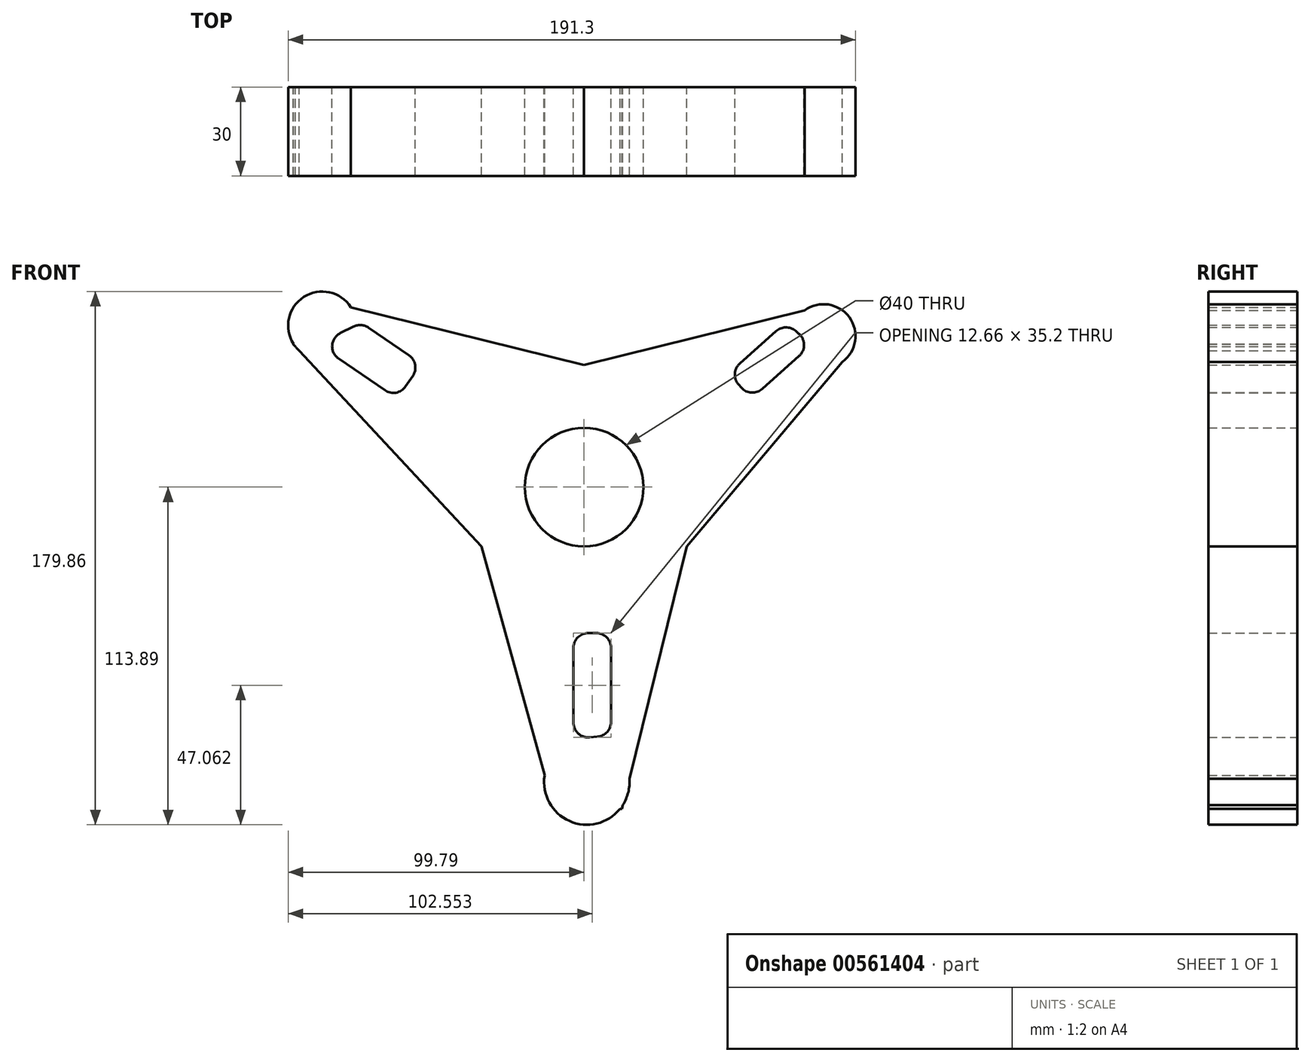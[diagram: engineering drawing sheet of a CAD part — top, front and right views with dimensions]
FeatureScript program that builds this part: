
annotation { "Feature Type Name" : "Feature", "Feature Type Description" : "" }
export const myFeature = defineFeature(function(context is Context, id is Id, definition is map)
    precondition{}
    {
        {
            var Q0;
            Q0=qCreatedBy(makeId("Front.planeOp"),FACE);
            var sketch = newSketch(context, id + "F0", { "sketchPlane" : qUnion([Q0])});
            skCircle(sketch, "E0", {"center": v(0, 0) * mm, "radius": 20 * mm});
            skCircle(sketch, "E1", {"center": v(0, 0) * mm, "radius": 40 * mm});
            skLineSegment(sketch, "E2", {"start": v(-3.57, -54.23) * mm, "end": v(-3.57, -79.44) * mm});
            skLineSegment(sketch, "E3", {"start": v(1.43, -49.23) * mm, "end": v(4.1, -49.23) * mm});
            skLineSegment(sketch, "E4", {"start": v(9.1, -54.23) * mm, "end": v(9.1, -79.23) * mm});
            skLineSegment(sketch, "E5", {"start": v(4.5, -84.21) * mm, "end": v(1.84, -84.43) * mm});
            skPoint(sketch, "E6.visualSharp", {"position": v(-3.57, -49.23) * mm});
            skArc(sketch, "E6.filletArc", {"start": v(1.43, -49.23) * mm, "mid": v(-2.1, -50.7) * mm, "end": v(-3.57, -54.23) * mm});
            skPoint(sketch, "E7.visualSharp", {"position": v(9.1, -49.23) * mm});
            skArc(sketch, "E7.filletArc", {"start": v(9.1, -54.23) * mm, "mid": v(7.63, -50.7) * mm, "end": v(4.1, -49.23) * mm});
            skPoint(sketch, "E8.visualSharp", {"position": v(9.1, -83.84) * mm});
            skArc(sketch, "E8.filletArc", {"start": v(4.5, -84.21) * mm, "mid": v(7.77, -82.62) * mm, "end": v(9.1, -79.23) * mm});
            skPoint(sketch, "E9.visualSharp", {"position": v(-3.57, -84.87) * mm});
            skArc(sketch, "E9.filletArc", {"start": v(-3.57, -79.44) * mm, "mid": v(-1.96, -83.12) * mm, "end": v(1.84, -84.43) * mm});
            skLineSegment(sketch, "E10", {"start": v(-72.68, 53.8) * mm, "end": v(-59.06, 44.46) * mm});
            skLineSegment(sketch, "E11", {"start": v(-57.76, 37.5) * mm, "end": v(-60.21, 33.94) * mm});
            skLineSegment(sketch, "E12", {"start": v(-67.17, 32.64) * mm, "end": v(-82.78, 43.35) * mm});
            skLineSegment(sketch, "E13", {"start": v(-82.17, 51.95) * mm, "end": v(-77.73, 54.16) * mm});
            skLineSegment(sketch, "E14", {"start": v(64.75, 52.59) * mm, "end": v(52.5, 41.65) * mm});
            skLineSegment(sketch, "E15", {"start": v(52.1, 34.6) * mm, "end": v(53.04, 33.54) * mm});
            skLineSegment(sketch, "E16", {"start": v(60.1, 33.14) * mm, "end": v(72.5, 44.22) * mm});
            skLineSegment(sketch, "E17", {"start": v(72.37, 51.8) * mm, "end": v(71.28, 52.7) * mm});
            skPoint(sketch, "E18.visualSharp", {"position": v(-75.1, 55.46) * mm});
            skArc(sketch, "E18.filletArc", {"start": v(-72.68, 53.8) * mm, "mid": v(-75.16, 54.67) * mm, "end": v(-77.73, 54.16) * mm});
            skPoint(sketch, "E19.visualSharp", {"position": v(-89.8, 48.17) * mm});
            skArc(sketch, "E19.filletArc", {"start": v(-82.17, 51.95) * mm, "mid": v(-84.94, 47.82) * mm, "end": v(-82.78, 43.35) * mm});
            skPoint(sketch, "E20.visualSharp", {"position": v(-63.04, 29.81) * mm});
            skArc(sketch, "E20.filletArc", {"start": v(-67.17, 32.64) * mm, "mid": v(-63.42, 31.85) * mm, "end": v(-60.21, 33.94) * mm});
            skPoint(sketch, "E21.visualSharp", {"position": v(-54.94, 41.63) * mm});
            skArc(sketch, "E21.filletArc", {"start": v(-57.76, 37.5) * mm, "mid": v(-56.97, 41.25) * mm, "end": v(-59.06, 44.46) * mm});
            skPoint(sketch, "E22.visualSharp", {"position": v(48.77, 38.32) * mm});
            skArc(sketch, "E22.filletArc", {"start": v(52.5, 41.65) * mm, "mid": v(50.84, 38.2) * mm, "end": v(52.1, 34.6) * mm});
            skPoint(sketch, "E23.visualSharp", {"position": v(56.37, 29.81) * mm});
            skArc(sketch, "E23.filletArc", {"start": v(53.04, 33.54) * mm, "mid": v(56.48, 31.88) * mm, "end": v(60.1, 33.14) * mm});
            skPoint(sketch, "E24.visualSharp", {"position": v(67.96, 55.46) * mm});
            skArc(sketch, "E24.filletArc", {"start": v(71.28, 52.7) * mm, "mid": v(68, 53.86) * mm, "end": v(64.75, 52.59) * mm});
            skPoint(sketch, "E25.visualSharp", {"position": v(76.83, 48.08) * mm});
            skArc(sketch, "E25.filletArc", {"start": v(72.5, 44.22) * mm, "mid": v(74.17, 48.03) * mm, "end": v(72.37, 51.8) * mm});
            skArc(sketch, "E26", {"start": v(-97.98, 48.3) * mm, "mid": v(-98, 48.24) * mm, "end": v(-98.04, 48.17) * mm});
            skLineSegment(sketch, "E27", {"start": v(-78.65, 60.68) * mm, "end": v(0, 41.2) * mm});
            skLineSegment(sketch, "E28", {"start": v(0, 41.2) * mm, "end": v(74.37, 59.62) * mm});
            skLineSegment(sketch, "E29", {"start": v(-98.04, 48.17) * mm, "end": v(-34.64, -20) * mm});
            skLineSegment(sketch, "E30", {"start": v(-34.64, -20) * mm, "end": v(-13.3, -97.28) * mm});
            skLineSegment(sketch, "E31", {"start": v(90.38, 46.14) * mm, "end": v(34.64, -20) * mm});
            skLineSegment(sketch, "E32", {"start": v(34.64, -20) * mm, "end": v(15.26, -98.33) * mm});
            skArc(sketch, "E33.trimOffspring", {"start": v(12.1, -108.56) * mm, "mid": v(12.42, -108.53) * mm, "end": v(12.75, -108.5) * mm});
            skArc(sketch, "E34", {"start": v(-78.65, 60.68) * mm, "mid": v(-95.71, 63.26) * mm, "end": v(-96.04, 46) * mm});
            skArc(sketch, "E35", {"start": v(87.1, 42.24) * mm, "mid": v(89.43, 57.3) * mm, "end": v(74.37, 59.62) * mm});
            skArc(sketch, "E36", {"start": v(-13.3, -97.28) * mm, "mid": v(0.39, -113.88) * mm, "end": v(15.26, -98.33) * mm});
            skLineSegment(sketch, "E37.trimOffspring", {"start": v(13.06, -107.22) * mm, "end": v(12.75, -108.5) * mm});
            skLineSegment(sketch, "E38", {"start": v(0, 0) * mm, "end": v(-34.64, -20) * mm});
            skLineSegment(sketch, "E39", {"start": v(0, 0) * mm, "end": v(34.64, -20) * mm});
            skLineSegment(sketch, "E40", {"start": v(0, 0) * mm, "end": v(0, 41.2) * mm});
            skSolve(sketch);
        }
        {
            var Q0;
            Q0 = qSketchRegion(id + "F0", true);
            extrude(context, id + "F1", {"entities" : qUnion([Q0]), "depth" : 30 * mm, "offsetDistance" : 25 * mm});
        }
    });
